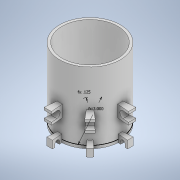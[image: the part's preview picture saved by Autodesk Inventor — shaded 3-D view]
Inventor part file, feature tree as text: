
AUTODESK INVENTOR PART (.ipt)
format: ipt  version: 2022 (Build 260153000, 153)  size: 199,680 bytes
history: native  units: in
note: dims shown in document units (in); Inventor stores cm internally (conversion verified against a paired STEP export)
features: sketch x4, extrude x2, revolve x2, pattern_circular x1
ambient origin geometry x8: Origin, YZ Plane, XZ Plane, XY Plane, X Axis, Y Axis, Z Axis, Center Point
bodies: Body1 (feature_tree)
feature tree (9):
  sketch  "Sketch8"  dims[d25=3.0in d26=0.125in]
  extrude  "Extrusion6"  Depth=0.125in
  extrude  "Extrusion7"  Depth=3.35in TaperAngle=0.0deg
  sketch  "Sketch9"  dims[d27=0.15in d28=0.0in d29=3.35in d30=0.0in]
  revolve  "Revolution1"  [1 undecoded]
  revolve  "Revolution2"  [1 undecoded]
  pattern_circular  "Circular Pattern2"  [2 undecoded]
  sketch  "Sketch10"  dims[d31=0.25in d32=0.125in]
  sketch  "Sketch11"  dims[d35=0.125in d36=0.125in d37=0.055in d38=0.3382in d39=0.125in d40=0.125in d41=0.125in d42=0.125in d43=0.0687in d44=1.25in d45=1.1811in d46=90.0deg]
note: 4 required parameter values undecoded (feature->parameter linkage not recoverable at this tier; creation-order binding heuristic only, values carry confidence <= 0.55)